# Revit family: Seating-LAMMHULTS-S70-3-Barstool
name_source: partatom
category: Furniture
revit_build: Autodesk Revit 2015 (Build: 20160512_0715(x64)
units: mm (PartAtom-declared; Revit-internal decimal feet)

## types (6) — shared parameters
Assembly Code = E2020
Depth = 480 mm  [stored 1.5748 ft]
Description = *Please enter mtrl description here for use in mto*
Height = 710 mm
Keynote = 46.B
Length = 480 mm  [stored 1.5748 ft]
Manufacturer = LAMMHULTS
URL = www.lammhults.se
Weight = 6.3 Kg
Width = 480 mm  [stored 1.5748 ft]

## per-type parameters (varying)
| type | Frame Material | Legs Material | Model | Seat Material |
| Black - Black | Colour - Black | Plastic - Black | S-70-3 | Colour - Black |
| Black - Wood | Colour - Black | Plastic - Black | S-70-3 | Wood - Veneer - Birch |
| Crome - Black | Metal - Chrome - Polished | Plastic - Black | S-70-3 | Colour - Black |
| Crome - Wood | Metal - Chrome - Polished | Plastic - Black | S-70-3 | Wood - Veneer - Birch |
| White - White | Colour - White | Plastic - White | S-70-4 | Colour - White |
| White - Wood | Colour - White | Plastic - White | S-70-5 | Wood - Veneer - Birch |

note: [stored X ft] marks values corroborated as IEEE doubles in the binary element streams (Revit-internal decimal feet)

## geometry (parser evidence)
native form markers: Blend x12, Sweep x3
no freeform markers — native parametric forms only
